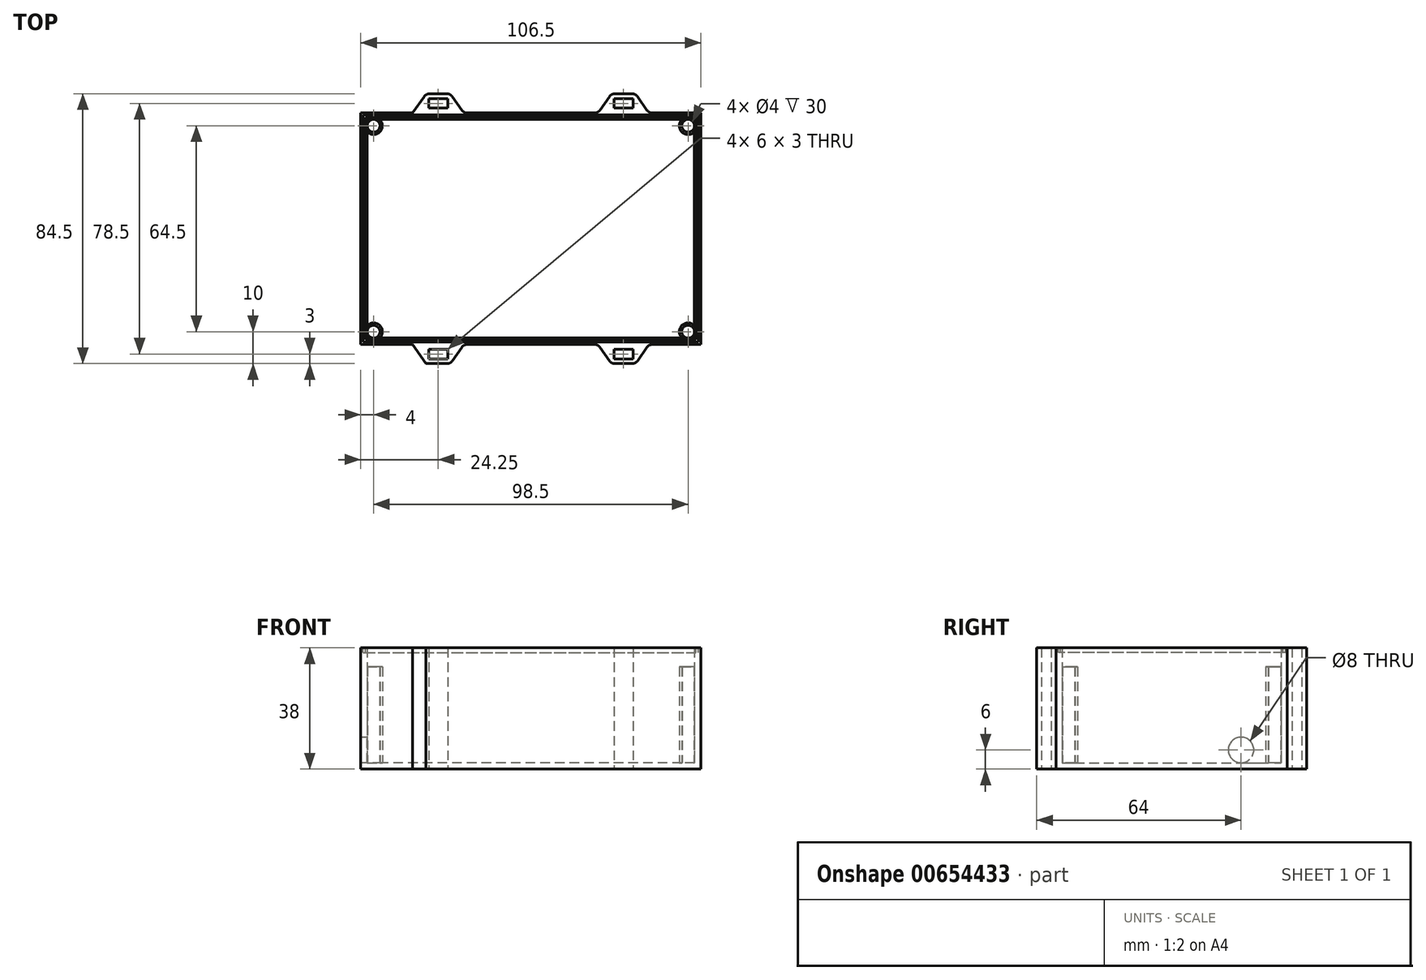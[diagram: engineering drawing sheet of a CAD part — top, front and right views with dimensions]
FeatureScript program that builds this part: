
annotation { "Feature Type Name" : "Feature", "Feature Type Description" : "" }
export const myFeature = defineFeature(function(context is Context, id is Id, definition is map)
    precondition{}
    {
        {
            var Q0;
            Q0=qCreatedBy(makeId("Top.planeOp"),FACE);
            var sketch = newSketch(context, id + "F0", { "sketchPlane" : qUnion([Q0])});
            skLineSegment(sketch, "E0.bottom", {"start": v(0, 0) * mm, "end": v(-106.5, 0) * mm});
            skLineSegment(sketch, "E0.top", {"start": v(0, 72.5) * mm, "end": v(-106.5, 72.5) * mm});
            skLineSegment(sketch, "E0.left", {"start": v(0, 0) * mm, "end": v(0, 72.5) * mm});
            skLineSegment(sketch, "E0.right", {"start": v(-106.5, 0) * mm, "end": v(-106.5, 72.5) * mm});
            skSolve(sketch);
        }
        {
            var Q0;
            Q0 = qSketchRegion(id + "F0", true);
            extrude(context, id + "F1", {"entities" : qUnion([Q0]), "depth" : 38 * mm, "offsetDistance" : 25 * mm});
        }
        {
            var Q0;
            Q0=makeQuery(id+"F1.opExtrude","CAP_FACE",FACE,{"disambiguationData":[OSD([sQuery(id+"F0.wireOp",EDGE,"E0.bottom"),sQuery(id+"F0.wireOp",EDGE,"E0.top"),sQuery(id+"F0.wireOp",EDGE,"E0.left"),sQuery(id+"F0.wireOp",EDGE,"E0.right")])],"isStart":false});
            shell(context, id + "F2", {"entities" : qUnion([Q0]), "thickness" : 2 * mm});
        }
        {
            var Q0;
            Q0=qCreatedBy(makeId("Top.planeOp"),FACE);
            var sketch = newSketch(context, id + "F3", { "sketchPlane" : qUnion([Q0])});
            skLineSegment(sketch, "E1", {"start": v(-53.25, 0) * mm, "end": v(-53.25, 61.9) * mm, "construction": true});
            skLineSegment(sketch, "E2", {"start": v(-32.25, 72.5) * mm, "end": v(-28.05, 78.5) * mm});
            skLineSegment(sketch, "E3", {"start": v(-28.05, 78.5) * mm, "end": v(-20.45, 78.5) * mm});
            skLineSegment(sketch, "E4", {"start": v(-20.45, 78.5) * mm, "end": v(-16.25, 72.5) * mm});
            skLineSegment(sketch, "E5", {"start": v(-16.25, 72.5) * mm, "end": v(-32.25, 72.5) * mm});
            skLineSegment(sketch, "E6.MirrorCS", {"start": v(-78.45, 78.5) * mm, "end": v(-86.05, 78.5) * mm});
            skLineSegment(sketch, "E7.MirrorCS", {"start": v(-86.05, 78.5) * mm, "end": v(-90.25, 72.5) * mm});
            skLineSegment(sketch, "E8.MirrorCS", {"start": v(-90.25, 72.5) * mm, "end": v(-74.25, 72.5) * mm});
            skLineSegment(sketch, "E9.MirrorCS", {"start": v(-74.25, 72.5) * mm, "end": v(-78.45, 78.5) * mm});
            skLineSegment(sketch, "E10.bottom", {"start": v(-27.25, 77) * mm, "end": v(-21.25, 77) * mm});
            skLineSegment(sketch, "E10.top", {"start": v(-27.25, 74) * mm, "end": v(-21.25, 74) * mm});
            skLineSegment(sketch, "E10.left", {"start": v(-27.25, 77) * mm, "end": v(-27.25, 74) * mm});
            skLineSegment(sketch, "E10.right", {"start": v(-21.25, 77) * mm, "end": v(-21.25, 74) * mm});
            skLineSegment(sketch, "E11.MirrorCS", {"start": v(-79.25, 77) * mm, "end": v(-85.25, 77) * mm});
            skLineSegment(sketch, "E12.MirrorCS", {"start": v(-79.25, 74) * mm, "end": v(-85.25, 74) * mm});
            skLineSegment(sketch, "E13.MirrorCS", {"start": v(-79.25, 77) * mm, "end": v(-79.25, 74) * mm});
            skLineSegment(sketch, "E14.MirrorCS", {"start": v(-85.25, 77) * mm, "end": v(-85.25, 74) * mm});
            skLineSegment(sketch, "E15", {"start": v(0, 36.25) * mm, "end": v(-96.7, 36.25) * mm, "construction": true});
            skLineSegment(sketch, "E16.MirrorCS", {"start": v(-79.25, -4.5) * mm, "end": v(-85.25, -4.5) * mm});
            skLineSegment(sketch, "E17.MirrorCS", {"start": v(-79.25, -1.5) * mm, "end": v(-85.25, -1.5) * mm});
            skLineSegment(sketch, "E18.MirrorCS", {"start": v(-85.25, -4.5) * mm, "end": v(-85.25, -1.5) * mm});
            skLineSegment(sketch, "E19.MirrorCS", {"start": v(-79.25, -4.5) * mm, "end": v(-79.25, -1.5) * mm});
            skLineSegment(sketch, "E20.MirrorCS", {"start": v(-90.25, 0) * mm, "end": v(-74.25, 0) * mm});
            skLineSegment(sketch, "E21.MirrorCS", {"start": v(-86.05, -6) * mm, "end": v(-90.25, 0) * mm});
            skLineSegment(sketch, "E22.MirrorCS", {"start": v(-74.25, 0) * mm, "end": v(-78.45, -6) * mm});
            skLineSegment(sketch, "E23.MirrorCS", {"start": v(-78.45, -6) * mm, "end": v(-86.05, -6) * mm});
            skLineSegment(sketch, "E24.MirrorCS", {"start": v(-21.25, -4.5) * mm, "end": v(-21.25, -1.5) * mm});
            skLineSegment(sketch, "E25.MirrorCS", {"start": v(-28.05, -6) * mm, "end": v(-20.45, -6) * mm});
            skLineSegment(sketch, "E26.MirrorCS", {"start": v(-27.25, -4.5) * mm, "end": v(-27.25, -1.5) * mm});
            skLineSegment(sketch, "E27.MirrorCS", {"start": v(-20.45, -6) * mm, "end": v(-16.25, 0) * mm});
            skLineSegment(sketch, "E28.MirrorCS", {"start": v(-27.25, -1.5) * mm, "end": v(-21.25, -1.5) * mm});
            skLineSegment(sketch, "E29.MirrorCS", {"start": v(-27.25, -4.5) * mm, "end": v(-21.25, -4.5) * mm});
            skLineSegment(sketch, "E30.MirrorCS", {"start": v(-16.25, 0) * mm, "end": v(-32.25, 0) * mm});
            skLineSegment(sketch, "E31.MirrorCS", {"start": v(-32.25, 0) * mm, "end": v(-28.05, -6) * mm});
            skSolve(sketch);
        }
        {
            var Q0;
            Q0 = qSketchRegion(id + "F3", true);
            extrude(context, id + "F4", {"entities" : qUnion([Q0]), "operationType" : NewBodyOperationType.ADD, "depth" : 38 * mm, "offsetDistance" : 25 * mm});
        }
        {
            var Q0;
            Q0=makeQuery(id+"F4.opExtrude","SWEPT_EDGE",EDGE,{"disambiguationData":[OSD([sQuery(id+"F3.wireOp",EDGE,"E6.MirrorCS"),sQuery(id+"F3.wireOp",EDGE,"E7.MirrorCS")])]});
            var Q1;
            Q1=makeQuery(id+"F4.opExtrude","SWEPT_EDGE",EDGE,{"disambiguationData":[OSD([sQuery(id+"F3.wireOp",EDGE,"E6.MirrorCS"),sQuery(id+"F3.wireOp",EDGE,"E9.MirrorCS")])]});
            var Q2;
            Q2=makeQuery(id+"F4.opExtrude","SWEPT_EDGE",EDGE,{"disambiguationData":[OSD([sQuery(id+"F3.wireOp",EDGE,"E8.MirrorCS"),sQuery(id+"F3.wireOp",EDGE,"E9.MirrorCS")])]});
            var Q3;
            Q3=makeQuery(id+"F4.opExtrude","SWEPT_EDGE",EDGE,{"disambiguationData":[OSD([sQuery(id+"F3.wireOp",EDGE,"E7.MirrorCS"),sQuery(id+"F3.wireOp",EDGE,"E8.MirrorCS")])]});
            var Q4;
            Q4=makeQuery(id+"F4.opExtrude","SWEPT_EDGE",EDGE,{"disambiguationData":[OSD([sQuery(id+"F3.wireOp",EDGE,"E2"),sQuery(id+"F3.wireOp",EDGE,"E5")])]});
            var Q5;
            Q5=makeQuery(id+"F4.opExtrude","SWEPT_EDGE",EDGE,{"disambiguationData":[OSD([sQuery(id+"F3.wireOp",EDGE,"E2"),sQuery(id+"F3.wireOp",EDGE,"E3")])]});
            var Q6;
            Q6=makeQuery(id+"F4.opExtrude","SWEPT_EDGE",EDGE,{"disambiguationData":[OSD([sQuery(id+"F3.wireOp",EDGE,"E3"),sQuery(id+"F3.wireOp",EDGE,"E4")])]});
            var Q7;
            Q7=makeQuery(id+"F4.opExtrude","SWEPT_EDGE",EDGE,{"disambiguationData":[OSD([sQuery(id+"F3.wireOp",EDGE,"E4"),sQuery(id+"F3.wireOp",EDGE,"E5")])]});
            var Q8;
            Q8=makeQuery(id+"F4.opExtrude","SWEPT_EDGE",EDGE,{"disambiguationData":[OSD([sQuery(id+"F3.wireOp",EDGE,"E20.MirrorCS"),sQuery(id+"F3.wireOp",EDGE,"E22.MirrorCS")])]});
            var Q9;
            Q9=makeQuery(id+"F4.opExtrude","SWEPT_EDGE",EDGE,{"disambiguationData":[OSD([sQuery(id+"F3.wireOp",EDGE,"E22.MirrorCS"),sQuery(id+"F3.wireOp",EDGE,"E23.MirrorCS")])]});
            var Q10;
            Q10=makeQuery(id+"F4.opExtrude","SWEPT_EDGE",EDGE,{"disambiguationData":[OSD([sQuery(id+"F3.wireOp",EDGE,"E20.MirrorCS"),sQuery(id+"F3.wireOp",EDGE,"E21.MirrorCS")])]});
            var Q11;
            Q11=makeQuery(id+"F4.opExtrude","SWEPT_EDGE",EDGE,{"disambiguationData":[OSD([sQuery(id+"F3.wireOp",EDGE,"E30.MirrorCS"),sQuery(id+"F3.wireOp",EDGE,"E31.MirrorCS")])]});
            var Q12;
            Q12=makeQuery(id+"F4.opExtrude","SWEPT_EDGE",EDGE,{"disambiguationData":[OSD([sQuery(id+"F3.wireOp",EDGE,"E25.MirrorCS"),sQuery(id+"F3.wireOp",EDGE,"E31.MirrorCS")])]});
            var Q13;
            Q13=makeQuery(id+"F4.opExtrude","SWEPT_EDGE",EDGE,{"disambiguationData":[OSD([sQuery(id+"F3.wireOp",EDGE,"E25.MirrorCS"),sQuery(id+"F3.wireOp",EDGE,"E27.MirrorCS")])]});
            var Q14;
            Q14=makeQuery(id+"F4.opExtrude","SWEPT_EDGE",EDGE,{"disambiguationData":[OSD([sQuery(id+"F3.wireOp",EDGE,"E27.MirrorCS"),sQuery(id+"F3.wireOp",EDGE,"E30.MirrorCS")])]});
            fillet(context, id + "F5", {"entities" : qUnion([Q0, Q1, Q2, Q3, Q4, Q5, Q6, Q7, Q8, Q9, Q10, Q11, Q12, Q13, Q14]), "radius" : 2 * mm, "tangentPropagation" : true, "allowEdgeOverflow" : false});
        }
        {
            var Q0;
            Q0=makeQuery(id+"F1.opExtrude","SWEPT_FACE",FACE,{"disambiguationData":[OSD([sQuery(id+"F0.wireOp",EDGE,"E0.right")])]});
            var sketch = newSketch(context, id + "F6", { "sketchPlane" : qUnion([Q0])});
            skCircle(sketch, "E32", {"center": v(-58, 6) * mm, "radius": 4 * mm});
            skSolve(sketch);
        }
        {
            var Q0;
            Q0 = qSketchRegion(id + "F6", true);
            extrude(context, id + "F7", {"entities" : qUnion([Q0]), "operationType" : NewBodyOperationType.REMOVE, "endBound" : BoundingType.UP_TO_NEXT, "oppositeDirection" : true, "depth" : 25 * mm, "offsetDistance" : 25 * mm});
        }
        {
            var Q0;
            Q0=makeQuery(id+"F2.opShell","OFFSET_FACE",FACE,{"disambiguationData":[OSD([sQuery(id+"F0.wireOp",EDGE,"E0.bottom"),sQuery(id+"F0.wireOp",EDGE,"E0.top"),sQuery(id+"F0.wireOp",EDGE,"E0.left"),sQuery(id+"F0.wireOp",EDGE,"E0.right")])]});
            var sketch = newSketch(context, id + "F8", { "sketchPlane" : qUnion([Q0])});
            skCircle(sketch, "E33", {"center": v(-102.5, 68.5) * mm, "radius": 2.75 * mm});
            skCircle(sketch, "E34", {"center": v(-102.5, 68.5) * mm, "radius": 2 * mm});
            skLineSegment(sketch, "E35", {"start": v(-53.25, 70.5) * mm, "end": v(-53.25, 2) * mm, "construction": true});
            skLineSegment(sketch, "E36", {"start": v(-2, 36.25) * mm, "end": v(-104.5, 36.25) * mm, "construction": true});
            skPoint(sketch, "E36.endSnap0", {"position": v(-104.5, 30) * mm});
            skCircle(sketch, "E37.MirrorC", {"center": v(-4, 68.5) * mm, "radius": 2 * mm});
            skCircle(sketch, "E38.MirrorC", {"center": v(-4, 68.5) * mm, "radius": 2.75 * mm});
            skCircle(sketch, "E39.MirrorC", {"center": v(-4, 4) * mm, "radius": 2.75 * mm});
            skCircle(sketch, "E40.MirrorC", {"center": v(-4, 4) * mm, "radius": 2 * mm});
            skCircle(sketch, "E41.MirrorC", {"center": v(-102.5, 4) * mm, "radius": 2 * mm});
            skCircle(sketch, "E42.MirrorC", {"center": v(-102.5, 4) * mm, "radius": 2.75 * mm});
            skSolve(sketch);
        }
        {
            var Q0;
            Q0 = qSketchRegion(id + "F8", true);
            extrude(context, id + "F9", {"entities" : qUnion([Q0]), "operationType" : NewBodyOperationType.ADD, "depth" : 30 * mm, "offsetDistance" : 25 * mm});
        }
        {
            var Q0;
            Q0=makeQuery(id+"F4.boolean.opBoolean","MERGE",FACE,{"derivedFrom":[makeQuery(id+"F1.opExtrude","CAP_FACE",FACE,{"disambiguationData":[OSD([sQuery(id+"F0.wireOp",EDGE,"E0.bottom"),sQuery(id+"F0.wireOp",EDGE,"E0.top"),sQuery(id+"F0.wireOp",EDGE,"E0.left"),sQuery(id+"F0.wireOp",EDGE,"E0.right")])],"isStart":false}),makeQuery(id+"F4.opExtrude","CAP_FACE",FACE,{"disambiguationData":[OSD([sQuery(id+"F3.wireOp",EDGE,"E2"),sQuery(id+"F3.wireOp",EDGE,"E3"),sQuery(id+"F3.wireOp",EDGE,"E4"),sQuery(id+"F3.wireOp",EDGE,"E5"),sQuery(id+"F3.wireOp",EDGE,"E10.bottom"),sQuery(id+"F3.wireOp",EDGE,"E10.top"),sQuery(id+"F3.wireOp",EDGE,"E10.left"),sQuery(id+"F3.wireOp",EDGE,"E10.right")])],"isStart":false}),makeQuery(id+"F4.opExtrude","CAP_FACE",FACE,{"disambiguationData":[OSD([sQuery(id+"F3.wireOp",EDGE,"E6.MirrorCS"),sQuery(id+"F3.wireOp",EDGE,"E7.MirrorCS"),sQuery(id+"F3.wireOp",EDGE,"E8.MirrorCS"),sQuery(id+"F3.wireOp",EDGE,"E9.MirrorCS"),sQuery(id+"F3.wireOp",EDGE,"E11.MirrorCS"),sQuery(id+"F3.wireOp",EDGE,"E12.MirrorCS"),sQuery(id+"F3.wireOp",EDGE,"E13.MirrorCS"),sQuery(id+"F3.wireOp",EDGE,"E14.MirrorCS")])],"isStart":false}),makeQuery(id+"F4.opExtrude","CAP_FACE",FACE,{"disambiguationData":[OSD([sQuery(id+"F3.wireOp",EDGE,"E16.MirrorCS"),sQuery(id+"F3.wireOp",EDGE,"E17.MirrorCS"),sQuery(id+"F3.wireOp",EDGE,"E18.MirrorCS"),sQuery(id+"F3.wireOp",EDGE,"E19.MirrorCS"),sQuery(id+"F3.wireOp",EDGE,"E20.MirrorCS"),sQuery(id+"F3.wireOp",EDGE,"E21.MirrorCS"),sQuery(id+"F3.wireOp",EDGE,"E22.MirrorCS"),sQuery(id+"F3.wireOp",EDGE,"E23.MirrorCS")])],"isStart":false}),makeQuery(id+"F4.opExtrude","CAP_FACE",FACE,{"disambiguationData":[OSD([sQuery(id+"F3.wireOp",EDGE,"E24.MirrorCS"),sQuery(id+"F3.wireOp",EDGE,"E25.MirrorCS"),sQuery(id+"F3.wireOp",EDGE,"E26.MirrorCS"),sQuery(id+"F3.wireOp",EDGE,"E27.MirrorCS"),sQuery(id+"F3.wireOp",EDGE,"E28.MirrorCS"),sQuery(id+"F3.wireOp",EDGE,"E29.MirrorCS"),sQuery(id+"F3.wireOp",EDGE,"E30.MirrorCS"),sQuery(id+"F3.wireOp",EDGE,"E31.MirrorCS")])],"isStart":false})]});
            var sketch = newSketch(context, id + "F10", { "sketchPlane" : qUnion([Q0])});
            skLineSegment(sketch, "E43.bottom", {"start": v(-105, 71.12) * mm, "end": v(-1.5, 71.12) * mm});
            skLineSegment(sketch, "E43.top", {"start": v(-105, 1.5) * mm, "end": v(-1.5, 1.5) * mm});
            skLineSegment(sketch, "E43.left", {"start": v(-105, 71.12) * mm, "end": v(-105, 1.5) * mm});
            skLineSegment(sketch, "E43.right", {"start": v(-1.5, 71.12) * mm, "end": v(-1.5, 1.5) * mm});
            skLineSegment(sketch, "E44.0", {"start": v(-105.75, 71.87) * mm, "end": v(-0.75, 71.87) * mm});
            skLineSegment(sketch, "E44.1", {"start": v(-105.75, 71.87) * mm, "end": v(-105.75, 0.75) * mm});
            skLineSegment(sketch, "E44.2", {"start": v(-105.75, 0.75) * mm, "end": v(-0.75, 0.75) * mm});
            skLineSegment(sketch, "E44.3", {"start": v(-0.75, 71.88) * mm, "end": v(-0.75, 0.75) * mm});
            skSolve(sketch);
        }
        {
            var Q0;
            Q0 = qSketchRegion(id + "F10", true);
            extrude(context, id + "F11", {"entities" : qUnion([Q0]), "operationType" : NewBodyOperationType.REMOVE, "oppositeDirection" : true, "depth" : 1.5 * mm, "offsetDistance" : 25 * mm});
        }
    });
